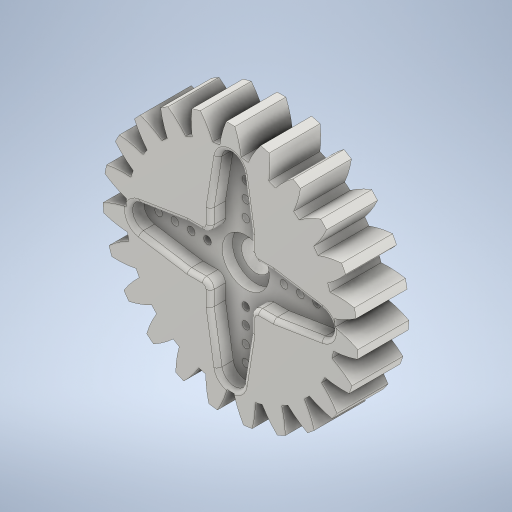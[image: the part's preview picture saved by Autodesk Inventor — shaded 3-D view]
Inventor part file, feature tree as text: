
AUTODESK INVENTOR PART (.ipt)
format: ipt  version: 2024.1 (Build 281209000, 209)  size: 602,624 bytes
history: native  units: mm (DEFAULTED — no unit token found)
features: extrude x4, sketch x4, plane x3, other x3, fillet x1
ambient origin geometry x8: Origin, YZ Plane, XZ Plane, XY Plane, X Axis, Y Axis, Z Axis, Center Point
bodies: Solid1 (feature_tree)
feature tree (15):
  extrude  "Extrusion1"  Depth=10.0mm TaperAngle=0.0deg
  plane  "Work Plane2"
  plane  "Work Plane8"
  plane  "Work Plane9"
  other  "Engrenagem reta"
  extrude  "Extrusão2"  Depth=10.0mm TaperAngle=0.0deg
  extrude  "Extrusão3"  Depth=1.36591mm TaperAngle=0.0deg
  extrude  "Extrusão4"  TaperAngle=0.0deg  [1 undecoded]
  fillet  "Arredondamento1"  Radius=70.0mm
  sketch  "Sketch1"  dims[d0=50.0mm d1=10.0mm d2=0.0mm]
  other  "Srf1"
  sketch  "Esboço3"  dims[d3=46.0mm d4=10.0mm d5=0.0mm]
  sketch  "Esboço4"  dims[d16=70.0mm d17=0.0mm d34=1.36591mm]
  sketch  "Esboço5"  dims[d39=0.0mm d41=0.0mm d43=70.0mm d46=70.0mm d47=0.0mm d48=0.0mm d49=3.0mm d50=0.0mm d51=10.0mm d52=0.0mm d53=5.0mm d54=0.0mm d55=0.8mm]
  other  "Diâmetro do flanco"
note: 1 required parameter value undecoded (feature->parameter linkage not recoverable at this tier; creation-order binding heuristic only, values carry confidence <= 0.55)
